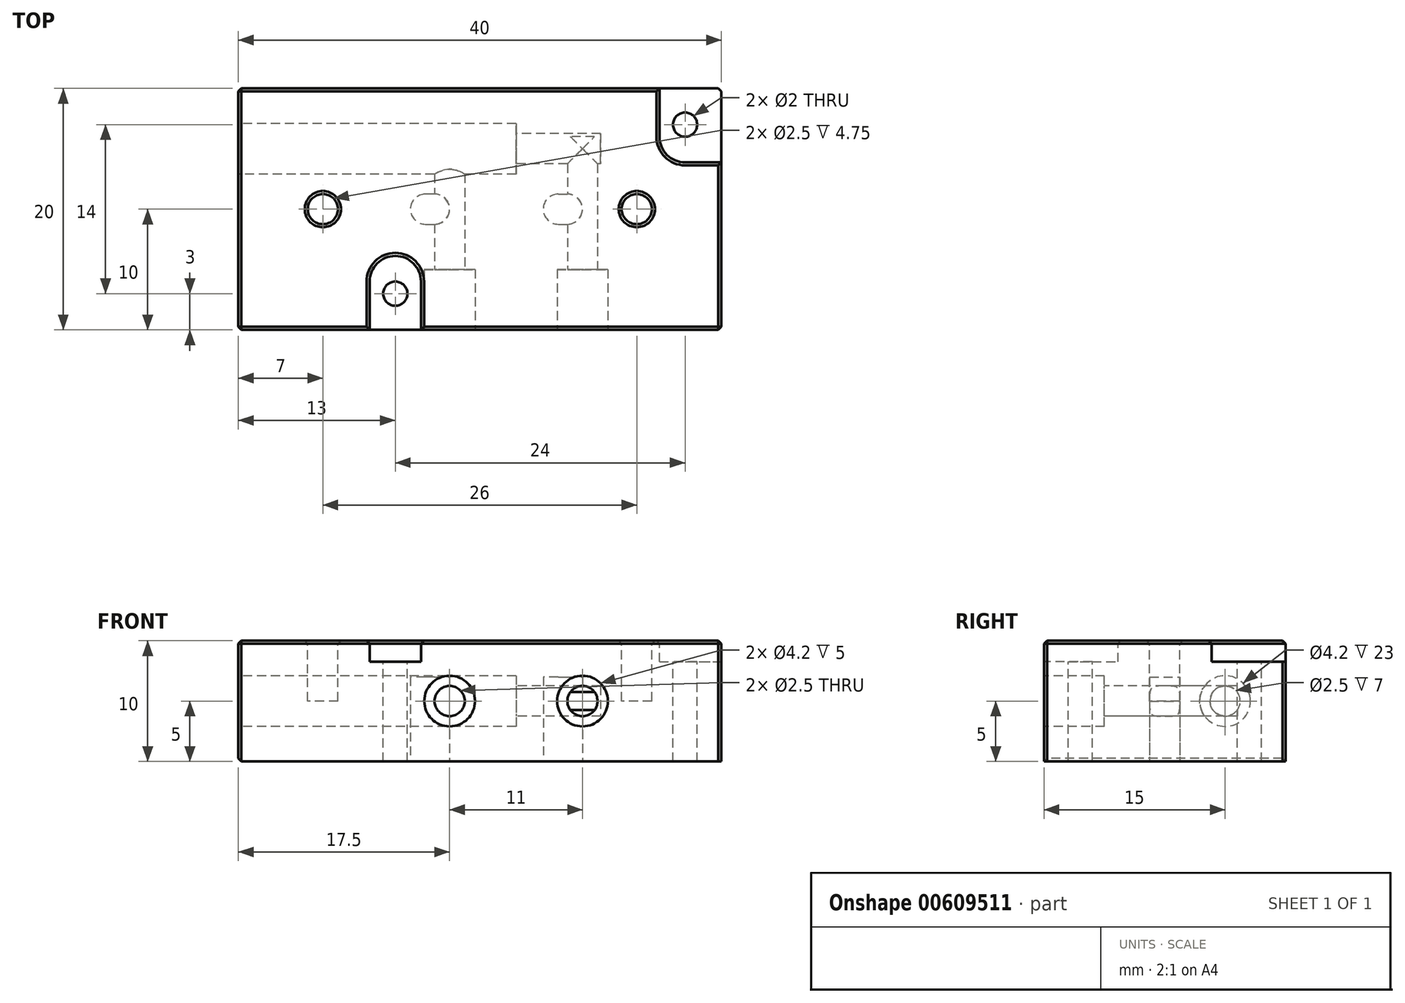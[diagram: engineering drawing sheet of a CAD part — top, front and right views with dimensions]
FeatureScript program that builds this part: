
annotation { "Feature Type Name" : "Feature", "Feature Type Description" : "" }
export const myFeature = defineFeature(function(context is Context, id is Id, definition is map)
    precondition{}
    {
        {
            var Q0;
            Q0=qCreatedBy(makeId("Top.planeOp"),FACE);
            var sketch = newSketch(context, id + "F0", { "sketchPlane" : qUnion([Q0])});
            skLineSegment(sketch, "E0.bottom", {"start": v(0, 0) * mm, "end": v(40, 0) * mm});
            skLineSegment(sketch, "E0.top", {"start": v(0, -20) * mm, "end": v(40, -20) * mm});
            skLineSegment(sketch, "E0.left", {"start": v(0, 0) * mm, "end": v(0, -20) * mm});
            skLineSegment(sketch, "E0.right", {"start": v(40, 0) * mm, "end": v(40, -20) * mm});
            skSolve(sketch);
        }
        {
            var Q0;
            Q0=makeQuery(id+"F0.imprint","IMPRINT",FACE,{"disambiguationData":[TD([[makeQuery(id+"F0.imprint","IMPRINT",EDGE,{"derivedFrom":sQuery(id+"F0.wireOp",EDGE,"E0.bottom")}),-1.0]])]});
            extrude(context, id + "F1", {"entities" : qUnion([Q0]), "depth" : 10 * mm, "offsetDistance" : 25 * mm});
        }
        {
            var Q0;
            Q0=makeQuery(id+"F1.opExtrude","SWEPT_FACE",FACE,{"disambiguationData":[OSD([sQuery(id+"F0.wireOp",EDGE,"E0.top")])]});
            var sketch = newSketch(context, id + "F2", { "sketchPlane" : qUnion([Q0])});
            skLineSegment(sketch, "E1", {"start": v(40, 5) * mm, "end": v(0, 5) * mm, "construction": true});
            skCircle(sketch, "E2", {"center": v(28.5, 5) * mm, "radius": 2.1 * mm});
            skCircle(sketch, "E3", {"center": v(17.5, 5) * mm, "radius": 2.1 * mm});
            skCircle(sketch, "E4", {"center": v(17.5, 5) * mm, "radius": 1.25 * mm});
            skCircle(sketch, "E5", {"center": v(28.5, 5) * mm, "radius": 1.25 * mm});
            skSolve(sketch);
        }
        {
            var Q0;
            Q0=makeQuery(id+"F2.imprint","IMPRINT",FACE,{"disambiguationData":[TD([[makeQuery(id+"F2.imprint","IMPRINT",EDGE,{"derivedFrom":sQuery(id+"F2.wireOp",EDGE,"E2")}),1.0]])]});
            var Q1;
            Q1=makeQuery(id+"F2.imprint","IMPRINT",FACE,{"disambiguationData":[TD([[makeQuery(id+"F2.imprint","IMPRINT",EDGE,{"derivedFrom":sQuery(id+"F2.wireOp",EDGE,"E3")}),1.0]])]});
            extrude(context, id + "F3", {"entities" : qUnion([Q0, Q1]), "operationType" : NewBodyOperationType.REMOVE, "oppositeDirection" : true, "depth" : 5 * mm, "offsetDistance" : 25 * mm});
        }
        {
            var Q0;
            Q0=makeQuery(id+"F1.opExtrude","CAP_FACE",FACE,{"disambiguationData":[OSD([sQuery(id+"F0.wireOp",EDGE,"E0.bottom"),sQuery(id+"F0.wireOp",EDGE,"E0.top"),sQuery(id+"F0.wireOp",EDGE,"E0.left"),sQuery(id+"F0.wireOp",EDGE,"E0.right")])],"isStart":false});
            var sketch = newSketch(context, id + "F4", { "sketchPlane" : qUnion([Q0])});
            skLineSegment(sketch, "E6", {"start": v(40, -10) * mm, "end": v(0, -10) * mm, "construction": true});
            skCircle(sketch, "E7", {"center": v(26.5, -10) * mm, "radius": 1.25 * mm});
            skCircle(sketch, "E8", {"center": v(15.5, -10) * mm, "radius": 1.25 * mm});
            skCircle(sketch, "E9", {"center": v(26.5, -10) * mm, "radius": 3 * mm});
            skCircle(sketch, "E10", {"center": v(15.5, -10) * mm, "radius": 3 * mm});
            skLineSegment(sketch, "E11", {"start": v(37, -20) * mm, "end": v(37, -3) * mm, "construction": true});
            skLineSegment(sketch, "E12", {"start": v(37, -3) * mm, "end": v(40, -3) * mm, "construction": true});
            skLineSegment(sketch, "E13", {"start": v(0, -17) * mm, "end": v(13, -17) * mm, "construction": true});
            skLineSegment(sketch, "E14", {"start": v(13, -17) * mm, "end": v(13, 0) * mm, "construction": true});
            skCircle(sketch, "E15", {"center": v(13, -17) * mm, "radius": 1 * mm});
            skCircle(sketch, "E16", {"center": v(37, -3) * mm, "radius": 1 * mm});
            skArc(sketch, "E17", {"start": v(15.13, -16) * mm, "mid": v(13, -13.88) * mm, "end": v(10.88, -16) * mm});
            skLineSegment(sketch, "E18", {"start": v(10.88, -16) * mm, "end": v(10.88, -20) * mm});
            skLineSegment(sketch, "E19", {"start": v(15.13, -16) * mm, "end": v(15.13, -20) * mm});
            skArc(sketch, "E20", {"start": v(34.88, -4) * mm, "mid": v(35.5, -5.5) * mm, "end": v(37, -6.12) * mm});
            skLineSegment(sketch, "E21", {"start": v(37, -6.12) * mm, "end": v(40, -6.12) * mm});
            skLineSegment(sketch, "E22", {"start": v(34.88, -4) * mm, "end": v(34.88, 0) * mm});
            skSolve(sketch);
        }
        {
            var Q0;
            Q0=makeQuery(id+"F1.opExtrude","CAP_FACE",FACE,{"disambiguationData":[OSD([sQuery(id+"F0.wireOp",EDGE,"E0.bottom"),sQuery(id+"F0.wireOp",EDGE,"E0.top"),sQuery(id+"F0.wireOp",EDGE,"E0.left"),sQuery(id+"F0.wireOp",EDGE,"E0.right")])],"isStart":true});
            var sketch = newSketch(context, id + "F5", { "sketchPlane" : qUnion([Q0])});
            skLineSegment(sketch, "E23.bottom", {"start": v(-8.36, -7.93) * mm, "end": v(37.73, -7.93) * mm});
            skLineSegment(sketch, "E23.top", {"start": v(-8.36, 26.65) * mm, "end": v(37.73, 26.65) * mm});
            skLineSegment(sketch, "E23.left", {"start": v(-8.36, -7.93) * mm, "end": v(-8.36, 26.65) * mm});
            skLineSegment(sketch, "E23.right", {"start": v(37.73, -7.93) * mm, "end": v(37.73, 26.65) * mm});
            skSolve(sketch);
        }
        {
            var Q0;
            Q0=makeQuery(id+"F4.imprint","IMPRINT",FACE,{"disambiguationData":[TD([[makeQuery(id+"F4.imprint","IMPRINT",EDGE,{"derivedFrom":sQuery(id+"F4.wireOp",EDGE,"E15")}),1.0]])]});
            var Q1;
            Q1=makeQuery(id+"F4.imprint","IMPRINT",FACE,{"disambiguationData":[TD([[makeQuery(id+"F4.imprint","IMPRINT",EDGE,{"derivedFrom":sQuery(id+"F4.wireOp",EDGE,"E16")}),1.0]])]});
            extrude(context, id + "F6", {"entities" : qUnion([Q0, Q1]), "operationType" : NewBodyOperationType.REMOVE, "oppositeDirection" : true, "depth" : 25 * mm, "offsetDistance" : 25 * mm});
        }
        {
            var Q0;
            Q0=makeQuery(id+"F1.opExtrude","CAP_FACE",FACE,{"disambiguationData":[OSD([sQuery(id+"F0.wireOp",EDGE,"E0.bottom"),sQuery(id+"F0.wireOp",EDGE,"E0.top"),sQuery(id+"F0.wireOp",EDGE,"E0.left"),sQuery(id+"F0.wireOp",EDGE,"E0.right")])],"isStart":true});
            var sketch = newSketch(context, id + "F7", { "sketchPlane" : qUnion([Q0])});
            skLineSegment(sketch, "E24", {"start": v(40, 10) * mm, "end": v(0, 10) * mm, "construction": true});
            skArc(sketch, "E25", {"start": v(15.5, 11.25) * mm, "mid": v(14.25, 10) * mm, "end": v(15.5, 8.75) * mm});
            skArc(sketch, "E26", {"start": v(16.25, 8.75) * mm, "mid": v(17.5, 10) * mm, "end": v(16.25, 11.25) * mm});
            skArc(sketch, "E27", {"start": v(26.5, 11.25) * mm, "mid": v(25.25, 10) * mm, "end": v(26.5, 8.75) * mm});
            skArc(sketch, "E28", {"start": v(27.25, 8.75) * mm, "mid": v(28.5, 10) * mm, "end": v(27.25, 11.25) * mm});
            skLineSegment(sketch, "E29", {"start": v(16.25, 8.75) * mm, "end": v(15.5, 8.75) * mm});
            skLineSegment(sketch, "E30", {"start": v(15.5, 11.25) * mm, "end": v(16.25, 11.25) * mm});
            skLineSegment(sketch, "E31", {"start": v(26.5, 8.75) * mm, "end": v(27.25, 8.75) * mm});
            skLineSegment(sketch, "E32", {"start": v(26.5, 11.25) * mm, "end": v(27.25, 11.25) * mm});
            skSolve(sketch);
        }
        {
            var Q0;
            Q0=makeQuery(id+"F7.imprint","IMPRINT",FACE,{"disambiguationData":[TD([[makeQuery(id+"F7.imprint","IMPRINT",EDGE,{"derivedFrom":sQuery(id+"F7.wireOp",EDGE,"385Feiqx-x298-DiUh-U1ex-ucgG066O05Ym")}),1.0]])]});
            var Q1;
            Q1=makeQuery(id+"F7.imprint","IMPRINT",FACE,{"disambiguationData":[TD([[makeQuery(id+"F7.imprint","IMPRINT",EDGE,{"derivedFrom":sQuery(id+"F7.wireOp",EDGE,"yAW7Hrj5-qFjP-1K4M-5UzZ-Dz1Le1THTDbW")}),1.0]])]});
            var Q2;
            Q2=makeQuery(id+"F7.imprint","IMPRINT",FACE,{"disambiguationData":[TD([[makeQuery(id+"F7.imprint","IMPRINT",EDGE,{"derivedFrom":sQuery(id+"F7.wireOp",EDGE,"E25")}),1.0]])]});
            var Q3;
            Q3=makeQuery(id+"F7.imprint","IMPRINT",FACE,{"disambiguationData":[TD([[makeQuery(id+"F7.imprint","IMPRINT",EDGE,{"derivedFrom":sQuery(id+"F7.wireOp",EDGE,"E27")}),1.0]])]});
            extrude(context, id + "F8", {"entities" : qUnion([Q0, Q1, Q2, Q3]), "operationType" : NewBodyOperationType.REMOVE, "oppositeDirection" : true, "depth" : 7 * mm, "offsetDistance" : 25 * mm});
        }
        {
            var Q0;
            Q0=makeQuery(id+"F1.opExtrude","SWEPT_FACE",FACE,{"disambiguationData":[OSD([sQuery(id+"F0.wireOp",EDGE,"E0.left")])]});
            var sketch = newSketch(context, id + "F9", { "sketchPlane" : qUnion([Q0])});
            skLineSegment(sketch, "E33", {"start": v(20, 5) * mm, "end": v(0, 5) * mm, "construction": true});
            skCircle(sketch, "E34", {"center": v(5, 5) * mm, "radius": 2.1 * mm});
            skCircle(sketch, "E35", {"center": v(5, 5) * mm, "radius": 1.25 * mm});
            skSolve(sketch);
        }
        {
            var Q0;
            Q0=makeQuery(id+"F4.imprint","IMPRINT",FACE,{"disambiguationData":[TD([[makeQuery(id+"F4.imprint","IMPRINT",EDGE,{"derivedFrom":sQuery(id+"F4.wireOp",EDGE,"E15")}),-1.0]])]});
            var Q1;
            Q1=makeQuery(id+"F4.imprint","IMPRINT",FACE,{"disambiguationData":[TD([[makeQuery(id+"F4.imprint","IMPRINT",EDGE,{"derivedFrom":sQuery(id+"F4.wireOp",EDGE,"E16")}),-1.0]])]});
            extrude(context, id + "F10", {"entities" : qUnion([Q0, Q1]), "operationType" : NewBodyOperationType.REMOVE, "oppositeDirection" : true, "depth" : 1.75 * mm, "offsetDistance" : 25 * mm});
        }
        {
            var Q0;
            Q0=makeQuery(id+"F9.imprint","IMPRINT",FACE,{"disambiguationData":[TD([[makeQuery(id+"F9.imprint","IMPRINT",EDGE,{"derivedFrom":sQuery(id+"F9.wireOp",EDGE,"E34")}),1.0]])]});
            extrude(context, id + "F11", {"entities" : qUnion([Q0]), "operationType" : NewBodyOperationType.REMOVE, "oppositeDirection" : true, "depth" : 23 * mm, "offsetDistance" : 25 * mm});
        }
        {
            var Q0;
            Q0=makeQuery(id+"F1.opExtrude","CAP_FACE",FACE,{"disambiguationData":[OSD([sQuery(id+"F0.wireOp",EDGE,"E0.bottom"),sQuery(id+"F0.wireOp",EDGE,"E0.top"),sQuery(id+"F0.wireOp",EDGE,"E0.left"),sQuery(id+"F0.wireOp",EDGE,"E0.right")])],"isStart":false});
            var sketch = newSketch(context, id + "F12", { "sketchPlane" : qUnion([Q0])});
            skLineSegment(sketch, "E36", {"start": v(0, -10) * mm, "end": v(40, -10) * mm, "construction": true});
            skCircle(sketch, "E37", {"center": v(7, -10) * mm, "radius": 1.25 * mm});
            skCircle(sketch, "E38", {"center": v(33, -10) * mm, "radius": 1.25 * mm});
            skSolve(sketch);
        }
        {
            var Q0;
            Q0=makeQuery(id+"F12.imprint","IMPRINT",FACE,{"disambiguationData":[TD([[makeQuery(id+"F12.imprint","IMPRINT",EDGE,{"derivedFrom":sQuery(id+"F12.wireOp",EDGE,"E37")}),1.0]])]});
            var Q1;
            Q1=makeQuery(id+"F12.imprint","IMPRINT",FACE,{"disambiguationData":[TD([[makeQuery(id+"F12.imprint","IMPRINT",EDGE,{"derivedFrom":sQuery(id+"F12.wireOp",EDGE,"E38")}),1.0]])]});
            extrude(context, id + "F13", {"entities" : qUnion([Q0, Q1]), "operationType" : NewBodyOperationType.REMOVE, "oppositeDirection" : true, "depth" : 5 * mm, "offsetDistance" : 25 * mm});
        }
        {
            var Q0;
            Q0=makeQuery(id+"F3.boolean.opBoolean","COPY",EDGE,{"derivedFrom":makeQuery(id+"F3.opExtrude","CAP_EDGE",EDGE,{"disambiguationData":[OSD([sQuery(id+"F2.wireOp",EDGE,"E3")])],"isStart":true})});
            var Q1;
            Q1=makeQuery(id+"F3.boolean.opBoolean","COPY",EDGE,{"derivedFrom":makeQuery(id+"F3.opExtrude","CAP_EDGE",EDGE,{"disambiguationData":[OSD([sQuery(id+"F2.wireOp",EDGE,"E2")])],"isStart":true})});
            var Q2;
            Q2=makeQuery(id+"F1.opExtrude","SWEPT_EDGE",EDGE,{"disambiguationData":[OSD([sQuery(id+"F0.wireOp",EDGE,"E0.bottom"),sQuery(id+"F0.wireOp",EDGE,"E0.left")])]});
            var Q3;
            Q3=makeQuery(id+"F1.opExtrude","SWEPT_EDGE",EDGE,{"disambiguationData":[OSD([sQuery(id+"F0.wireOp",EDGE,"E0.top"),sQuery(id+"F0.wireOp",EDGE,"E0.left")])]});
            var Q4;
            Q4=makeQuery(id+"F1.opExtrude","CAP_FACE",FACE,{"disambiguationData":[OSD([sQuery(id+"F0.wireOp",EDGE,"E0.bottom"),sQuery(id+"F0.wireOp",EDGE,"E0.top"),sQuery(id+"F0.wireOp",EDGE,"E0.left"),sQuery(id+"F0.wireOp",EDGE,"E0.right")])],"isStart":false});
            var Q5;
            Q5=makeQuery(id+"F1.opExtrude","CAP_EDGE",EDGE,{"disambiguationData":[OSD([sQuery(id+"F0.wireOp",EDGE,"E0.left")])],"isStart":true});
            var Q6;
            Q6=makeQuery(id+"F1.opExtrude","SWEPT_EDGE",EDGE,{"disambiguationData":[OSD([sQuery(id+"F0.wireOp",EDGE,"E0.top"),sQuery(id+"F0.wireOp",EDGE,"E0.right")])]});
            var Q7;
            Q7=makeQuery(id+"F1.opExtrude","SWEPT_EDGE",EDGE,{"disambiguationData":[OSD([sQuery(id+"F0.wireOp",EDGE,"E0.bottom"),sQuery(id+"F0.wireOp",EDGE,"E0.right")])]});
            var Q8;
            Q8=makeQuery(id+"F11.boolean.opBoolean","COPY",EDGE,{"derivedFrom":makeQuery(id+"F11.opExtrude","CAP_EDGE",EDGE,{"disambiguationData":[OSD([sQuery(id+"F9.wireOp",EDGE,"E34")])],"isStart":true})});
            chamfer(context, id + "F14", {"entities" : qUnion([Q0, Q1, Q2, Q3, Q4, Q5, Q6, Q7, Q8]), "width" : 0.25 * mm, "tangentPropagation" : true});
        }
        {
            var Q0;
            Q0=makeQuery(id+"F11.boolean.opBoolean","SPLIT",FACE,{"disambiguationData":[TD([makeQuery(id+"F11.opExtrude","SWEPT_FACE",FACE,{"disambiguationData":[OSD([sQuery(id+"F9.wireOp",EDGE,"E35")])]})])],"derivedFrom":makeQuery(id+"F1.opExtrude","SWEPT_FACE",FACE,{"disambiguationData":[OSD([sQuery(id+"F0.wireOp",EDGE,"E0.left")])]})});
            extrude(context, id + "F15", {"entities" : qUnion([Q0]), "operationType" : NewBodyOperationType.REMOVE, "oppositeDirection" : true, "depth" : 30 * mm, "offsetDistance" : 25 * mm});
        }
        {
            var Q0;
            Q0=makeQuery(id+"F3.boolean.opBoolean","SPLIT",FACE,{"disambiguationData":[TD([makeQuery(id+"F3.opExtrude","SWEPT_FACE",FACE,{"disambiguationData":[OSD([sQuery(id+"F2.wireOp",EDGE,"E4")])]})])],"derivedFrom":makeQuery(id+"F1.opExtrude","SWEPT_FACE",FACE,{"disambiguationData":[OSD([sQuery(id+"F0.wireOp",EDGE,"E0.top")])]})});
            var Q1;
            Q1=makeQuery(id+"F3.boolean.opBoolean","SPLIT",FACE,{"disambiguationData":[TD([makeQuery(id+"F3.opExtrude","SWEPT_FACE",FACE,{"disambiguationData":[OSD([sQuery(id+"F2.wireOp",EDGE,"E5")])]})])],"derivedFrom":makeQuery(id+"F1.opExtrude","SWEPT_FACE",FACE,{"disambiguationData":[OSD([sQuery(id+"F0.wireOp",EDGE,"E0.top")])]})});
            extrude(context, id + "F16", {"entities" : qUnion([Q0, Q1]), "operationType" : NewBodyOperationType.REMOVE, "oppositeDirection" : true, "depth" : 16 * mm, "offsetDistance" : 25 * mm});
        }
    });
